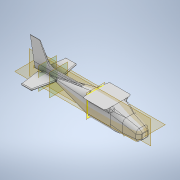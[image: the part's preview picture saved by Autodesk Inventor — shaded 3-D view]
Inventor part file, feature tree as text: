
AUTODESK INVENTOR PART (.ipt)
format: ipt  version: 2021 (Build 250183000, 183)  size: 4,286,976 bytes
history: native  units: mm
features: fillet x20, sketch x13, plane x9, other x7, loft x6, extrude x6, projected_geometry x4, chamfer x3
ambient origin geometry x8: Origin, YZ Plane, XZ Plane, XY Plane, X Axis, Y Axis, Z Axis, Center Point
bodies: Solid1 (feature_tree)
feature tree (68):
  sketch  "Sketch1"  dims[d0=884.936mm d1=835.0631mm d2=-901.954mm]
  plane  "Work Plane1"
  sketch  "Sketch2"  dims[d3=1072.134mm d4=93.599mm]
  plane  "Work Plane2"
  sketch  "Sketch3"  dims[d5=1118.87mm d6=-867.918mm d7=1225.296mm]
  plane  "Work Plane3"
  sketch  "Sketch4"  dims[d8=1519.682mm d9=76.581mm d10=-1718.818mm]
  loft  "Loft1"
  fillet  "Fillet1"  [1 undecoded]
  loft  "Loft2"
  loft  "Loft3"
  fillet  "Fillet2"  Radius=1225.296mm
  extrude  "Extrusion1"  Depth=76.581mm
  fillet  "Fillet3"  [1 undecoded]
  plane  "Work Plane4"
  sketch  "Sketch6"  dims[d18=0.0mm d19=90.0deg d20=0.0mm d21=90.0deg]
  sketch  "Sketch7"  dims[d22=0.0mm d23=90.0deg d24=127.0mm d25=254.0mm d26=-6.981317mm]
  extrude  "Extrusion2"  TaperAngle=0.0deg  [1 undecoded]
  fillet  "Fillet4"  Radius=254.0mm
  fillet  "Fillet5"  [1 undecoded]
  loft  "Loft4"
  plane  "Work Plane5"
  loft  "Loft5"
  fillet  "Fillet6"  Radius=254.0mm
  plane  "Work Plane6"
  extrude  "Extrusion3"  Depth=50.8mm
  fillet  "Fillet7"  Radius=357.378mm
  fillet  "Fillet8"  Radius=1225.296mm
  sketch  "Sketch10"  dims[d34=1.0mm d35=0.0mm d36=381.0mm]
  plane  "Work Plane7"
  loft  "Loft6"
  fillet  "Fillet9"  Radius=759.841mm
  plane  "Work Plane8"
  extrude  "Extrusion4"  Depth=381.0mm
  extrude  "Extrusion5"  TaperAngle=0.0deg  [1 undecoded]
  fillet  "Fillet10"  [1 undecoded]
  fillet  "Fillet11"  Radius=833.882mm
  fillet  "Fillet12"  Radius=153.162mm
  fillet  "Fillet13"  [1 undecoded]
  fillet  "Fillet14"  [1 undecoded]
  plane  "Work Plane9"
  extrude  "Extrusion6"  Depth=2000.0mm
  chamfer  "Chamfer1"  Distance=387.352mm
  chamfer  "Chamfer2"  Distance=600.0mm
  fillet  "Fillet15"  Radius=600.0mm
  fillet  "Fillet16"  Radius=1713.5mm
  fillet  "Fillet17"  Radius=127.0mm
  fillet  "Fillet18"  Radius=983.25mm
  fillet  "Fillet19"  Radius=25.4mm
  chamfer  "Chamfer3"  Distance=953.008mm
  fillet  "Fillet20"  [1 undecoded]
  other  "Edges1"
  other  "Edges2"
  sketch  "Sketch5"  dims[d11=0.0mm d12=90.0deg d13=0.0mm d14=90.0deg d15=254.0mm d16=0.0mm d17=90.0deg]
  projected_geometry  "Projected Loop1"
  projected_geometry  "Projected Loop2"
  projected_geometry  "Projected Loop3"
  other  "Edges3"
  other  "Edges4"
  sketch  "Sketch8"  dims[d27=50.8mm d28=2790.952mm d29=357.378mm d30=1225.296mm]
  other  "Edges5"
  sketch  "Sketch9"  dims[d31=612.648mm d32=1519.682mm d33=759.841mm]
  sketch  "Sketch11"  dims[d37=254.0mm d38=0.0mm d39=90.0deg d40=0.0mm d41=90.0deg d42=833.882mm d43=153.162mm d44=0.0mm d45=90.0deg d46=0.0mm d47=90.0deg]
  other  "Edges6"
  projected_geometry  "Projected Loop4"
  sketch  "Sketch12"  dims[d48=2189.25mm d49=2000.0mm]
  sketch  "Sketch14"  dims[d50=1225.296mm d51=387.352mm d52=600.0mm d53=600.0mm d54=1713.5mm d55=0.0mm d56=127.0mm d57=983.25mm d58=25.4mm d59=953.008mm d60=0.0mm d61=90.0deg d62=0.0mm d63=90.0deg d64=76.2mm d65=760.0mm d66=361.423629mm d67=411.296529mm d68=205.648265mm d69=180.711815mm d70=473.75mm d71=0.0mm d72=459.486mm d74=459.486mm d75=578.612mm d76=153.162mm d77=289.306mm d78=782.828mm d79=782.828mm d80=3403.6mm d81=1701.8mm d82=340.36mm d83=340.36mm d84=833.882mm d85=2.0mm d86=50.8mm d87=116.9162mm d88=0.0mm d89=50.8mm d90=50.8mm d91=38.1mm d92=38.1mm d93=38.1mm d107=-442.25mm d131=1923.034mm d135=1135.634mm d136=776.478mm d137=4064.0mm d138=1536.192mm d139=50.8mm d140=508.0mm d141=153.162mm d142=0.0mm d143=1546.05mm d144=63.5mm d145=45.0deg d146=1522.3mm d147=63.5mm d148=45.0deg d149=25.4mm d150=50.8mm d151=38.1mm d152=38.1mm d153=38.1mm d154=25.4mm d155=118.75mm d156=45.0deg d157=50.8mm]
  other  "Image2"
note: 9 required parameter values undecoded (feature->parameter linkage not recoverable at this tier; creation-order binding heuristic only, values carry confidence <= 0.55)
